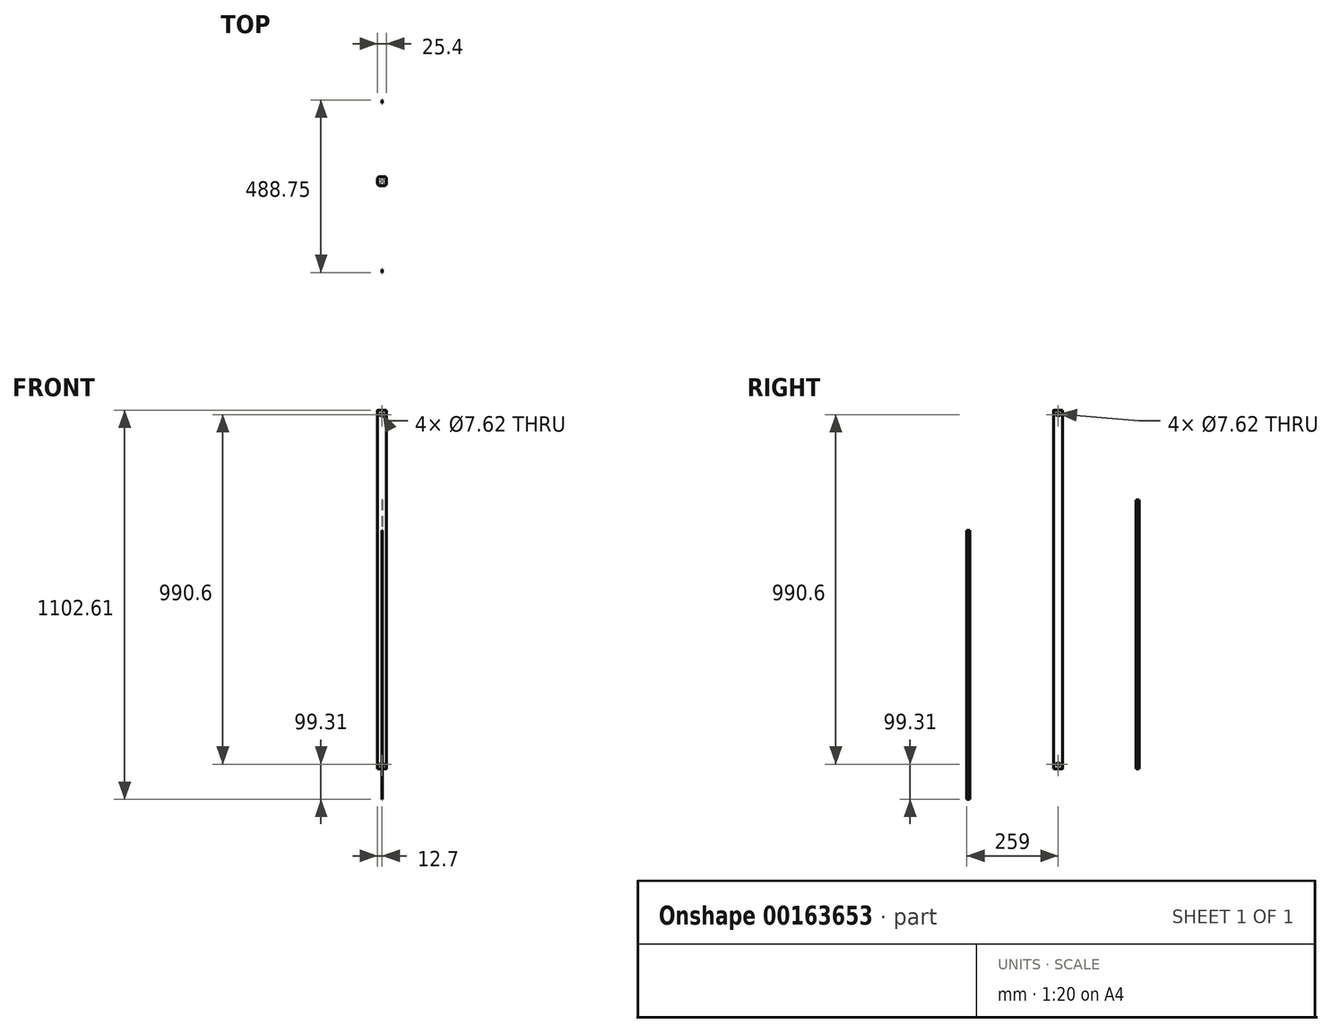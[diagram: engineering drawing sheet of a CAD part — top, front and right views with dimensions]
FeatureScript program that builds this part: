
annotation { "Feature Type Name" : "Feature", "Feature Type Description" : "" }
export const myFeature = defineFeature(function(context is Context, id is Id, definition is map)
    precondition{}
    {
        {
            var Q0;
            Q0=qCreatedBy(makeId("Top.planeOp"),FACE);
            var sketch = newSketch(context, id + "F0", { "sketchPlane" : qUnion([Q0])});
            skLineSegment(sketch, "E0.bottom", {"start": v(6.35, 12.7) * mm, "end": v(-6.35, 12.7) * mm});
            skLineSegment(sketch, "E0.top", {"start": v(6.35, -12.7) * mm, "end": v(-6.35, -12.7) * mm});
            skLineSegment(sketch, "E0.left", {"start": v(12.7, 6.35) * mm, "end": v(12.7, -6.35) * mm});
            skLineSegment(sketch, "E0.right", {"start": v(-12.7, 6.35) * mm, "end": v(-12.7, -6.35) * mm});
            skPoint(sketch, "E0.middle", {"position": v(0, 0) * mm});
            skPoint(sketch, "E1.visualSharp", {"position": v(-12.7, 12.7) * mm});
            skArc(sketch, "E1.filletArc", {"start": v(-6.35, 12.7) * mm, "mid": v(-10.84, 10.84) * mm, "end": v(-12.7, 6.35) * mm});
            skPoint(sketch, "E2.visualSharp", {"position": v(-12.7, -12.7) * mm});
            skArc(sketch, "E2.filletArc", {"start": v(-12.7, -6.35) * mm, "mid": v(-10.84, -10.84) * mm, "end": v(-6.35, -12.7) * mm});
            skPoint(sketch, "E3.visualSharp", {"position": v(12.7, -12.7) * mm});
            skArc(sketch, "E3.filletArc", {"start": v(6.35, -12.7) * mm, "mid": v(10.84, -10.84) * mm, "end": v(12.7, -6.35) * mm});
            skPoint(sketch, "E4.visualSharp", {"position": v(12.7, 12.7) * mm});
            skArc(sketch, "E4.filletArc", {"start": v(12.7, 6.35) * mm, "mid": v(10.84, 10.84) * mm, "end": v(6.35, 12.7) * mm});
            skSolve(sketch);
        }
        {
            var Q0;
            Q0=qSketchRegion(id+"F0",true);
            extrude(context, id + "F1", {"entities" : qUnion([Q0]), "depth" : 1016 * mm});
        }
        {
            var Q0;
            Q0=qCreatedBy(makeId("Right.planeOp"),FACE);
            var sketch = newSketch(context, id + "F2", { "sketchPlane" : qUnion([Q0])});
            skLineSegment(sketch, "E5.bottom", {"start": v(-259, 675.39) * mm, "end": v(-250.53, 675.39) * mm});
            skLineSegment(sketch, "E5.top", {"start": v(-259, -86.61) * mm, "end": v(-250.53, -86.61) * mm});
            skLineSegment(sketch, "E5.left", {"start": v(-259, 675.39) * mm, "end": v(-259, -86.61) * mm});
            skLineSegment(sketch, "E5.right", {"start": v(-250.53, 675.39) * mm, "end": v(-250.53, -86.61) * mm});
            skSolve(sketch);
        }
        {
            var Q0;
            Q0=makeQuery(id+"F2.imprint","IMPRINT",FACE,{"disambiguationData":[TD([[makeQuery(id+"F2.imprint","IMPRINT",EDGE,{"derivedFrom":sQuery(id+"F2.wireOp",EDGE,"E5.bottom")}),-1.0]])]});
            extrude(context, id + "F3", {"entities" : qUnion([Q0]), "depth" : 1.27 * mm});
        }
        {
            var Q0;
            Q0=qCreatedBy(makeId("Right.planeOp"),FACE);
            var sketch = newSketch(context, id + "F4", { "sketchPlane" : qUnion([Q0])});
            skLineSegment(sketch, "E6.bottom", {"start": v(221.29, 762) * mm, "end": v(229.75, 762) * mm});
            skLineSegment(sketch, "E6.top", {"start": v(221.29, 0) * mm, "end": v(229.75, 0) * mm});
            skLineSegment(sketch, "E6.left", {"start": v(221.29, 762) * mm, "end": v(221.29, 0) * mm});
            skLineSegment(sketch, "E6.right", {"start": v(229.75, 762) * mm, "end": v(229.75, 0) * mm});
            skSolve(sketch);
        }
        {
            var Q0;
            Q0=makeQuery(id+"F4.imprint","IMPRINT",FACE,{"disambiguationData":[TD([[makeQuery(id+"F4.imprint","IMPRINT",EDGE,{"derivedFrom":sQuery(id+"F4.wireOp",EDGE,"E6.bottom")}),-1.0]])]});
            var Q1;
            Q1=sQuery(id+"F4.wireOp",EDGE,"E6.right");
            var Q2;
            Q2=sQuery(id+"F4.wireOp",EDGE,"E6.left");
            var Q3;
            Q3=sQuery(id+"F4.wireOp",EDGE,"E6.top");
            var Q4;
            Q4=sQuery(id+"F4.wireOp",EDGE,"E6.bottom");
            extrude(context, id + "F5", {"entities" : qUnion([Q0]), "surfaceEntities" : qUnion([Q1, Q2, Q3, Q4]), "depth" : 1.27 * mm});
        }
        {
            var Q0;
            Q0=makeQuery(id+"F1.opExtrude","SWEPT_FACE",FACE,{"disambiguationData":[OSD([sQuery(id+"F0.wireOp",EDGE,"E0.top")])]});
            var sketch = newSketch(context, id + "F6", { "sketchPlane" : qUnion([Q0])});
            skLineSegment(sketch, "E7", {"start": v(0, 1016) * mm, "end": v(0, 1003.3) * mm});
            skPoint(sketch, "E7.endSnap0", {"position": v(0, 1016) * mm});
            skCircle(sketch, "E8", {"center": v(0, 1003.3) * mm, "radius": 3.81 * mm});
            skLineSegment(sketch, "E9", {"start": v(0, 0) * mm, "end": v(0, 12.7) * mm});
            skCircle(sketch, "E10", {"center": v(0, 12.7) * mm, "radius": 3.81 * mm});
            skSolve(sketch);
        }
        {
            var Q0;
            Q0=makeQuery(id+"F6.imprint","IMPRINT",FACE,{"disambiguationData":[TD([[makeQuery(id+"F6.imprint","IMPRINT",EDGE,{"derivedFrom":sQuery(id+"F6.wireOp",EDGE,"E8")}),1.0]])]});
            extrude(context, id + "F7", {"entities" : qUnion([Q0]), "operationType" : NewBodyOperationType.REMOVE, "oppositeDirection" : true, "depth" : 25.4 * mm});
        }
        {
            var Q0;
            Q0 = qSketchRegion(id + "F6", true);
            extrude(context, id + "F8", {"entities" : qUnion([Q0]), "operationType" : NewBodyOperationType.REMOVE, "oppositeDirection" : true, "depth" : 25.4 * mm});
        }
        {
            var Q0;
            Q0=makeQuery(id+"F1.opExtrude","SWEPT_FACE",FACE,{"disambiguationData":[OSD([sQuery(id+"F0.wireOp",EDGE,"E0.left")])]});
            var sketch = newSketch(context, id + "F9", { "sketchPlane" : qUnion([Q0])});
            skLineSegment(sketch, "E11", {"start": v(0, 0) * mm, "end": v(0, 12.7) * mm});
            skPoint(sketch, "E11.endSnap0", {"position": v(0, 0) * mm});
            skCircle(sketch, "E12", {"center": v(0, 12.7) * mm, "radius": 3.81 * mm});
            skLineSegment(sketch, "E13", {"start": v(0, 1016) * mm, "end": v(0, 1003.3) * mm});
            skPoint(sketch, "E13.endSnap0", {"position": v(0, 1016) * mm});
            skCircle(sketch, "E14", {"center": v(0, 1003.3) * mm, "radius": 3.81 * mm});
            skSolve(sketch);
        }
        {
            var Q0;
            Q0=makeQuery(id+"F9.imprint","IMPRINT",FACE,{"disambiguationData":[TD([[makeQuery(id+"F9.imprint","IMPRINT",EDGE,{"derivedFrom":sQuery(id+"F9.wireOp",EDGE,"E14")}),1.0]])]});
            var Q1;
            Q1=makeQuery(id+"F9.imprint","IMPRINT",FACE,{"disambiguationData":[TD([[makeQuery(id+"F9.imprint","IMPRINT",EDGE,{"derivedFrom":sQuery(id+"F9.wireOp",EDGE,"E12")}),1.0]])]});
            extrude(context, id + "F10", {"entities" : qUnion([Q0, Q1]), "operationType" : NewBodyOperationType.REMOVE, "oppositeDirection" : true, "depth" : 25.4 * mm});
        }
    });
